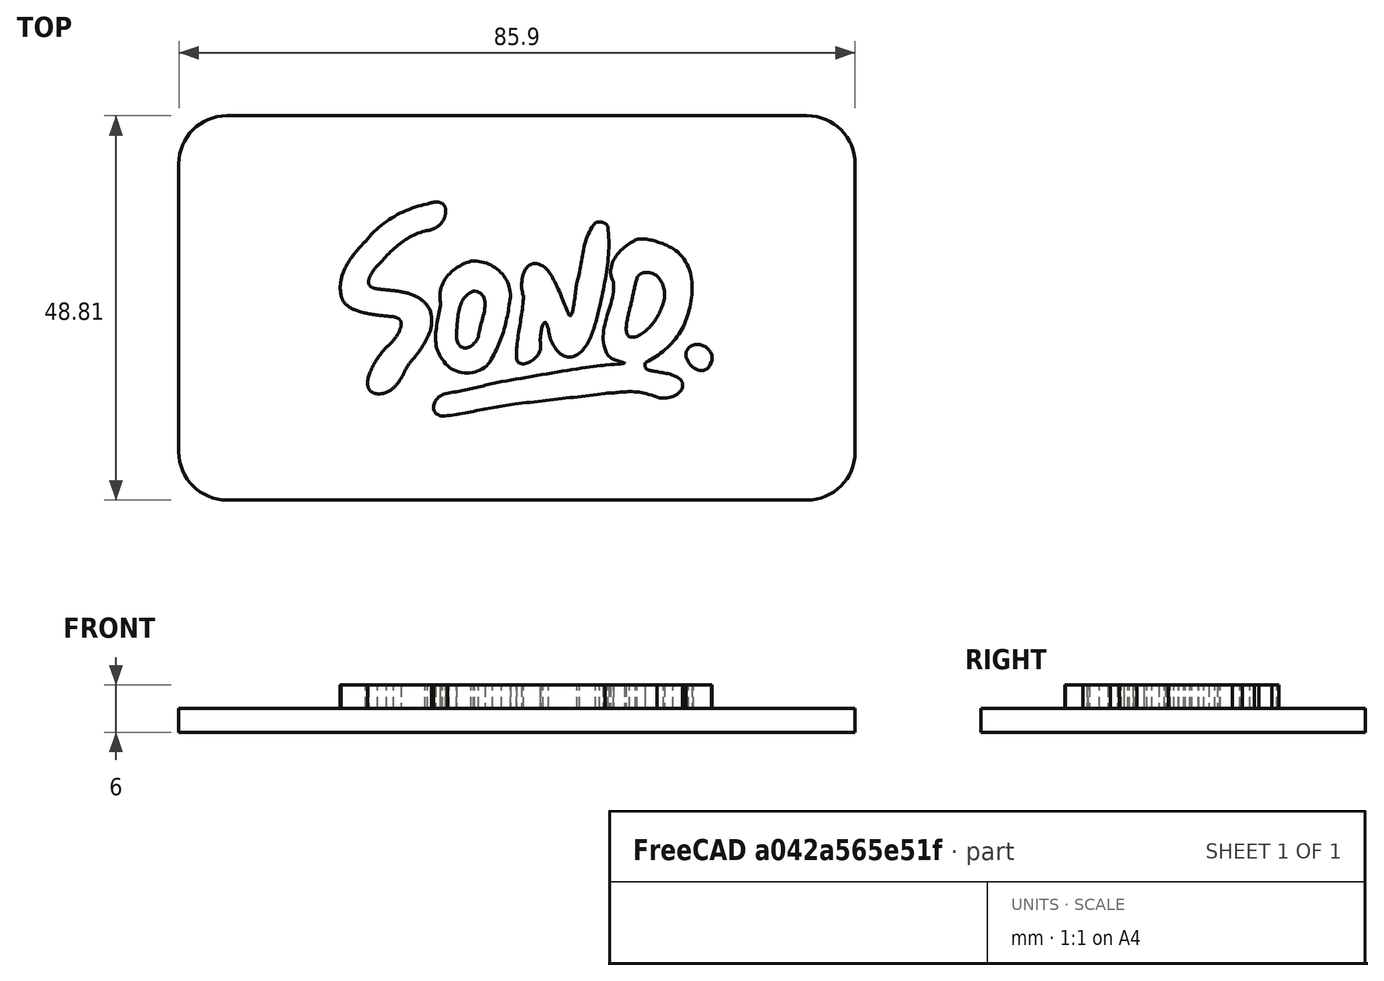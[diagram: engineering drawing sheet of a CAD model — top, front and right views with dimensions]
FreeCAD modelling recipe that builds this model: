
FCSTD DOCUMENT  (FreeCAD 0.22R37841 (Git))
Label: Sono
License: All rights reserved
LicenseURL: http://en.wikipedia.org/wiki/All_rights_reserved
objects: Sketcher::SketchObject×2, PartDesign::Pad×2, PartDesign::Body×1
note: 7 computed .brp shape members not serialized (recipe doc carries the construction recipe); baked Part::Feature solids carry a one-line shape summary decoded from their .brp

FEATURE [Sketcher::SketchObject] Sketch012
  AttachmentSupport = -> [XY_Plane]
  FullyConstrained = false
  MapMode = 5
  sketch-geometry (10):
    g0: LineSegment StartX=2989.09 StartY=-2800.65 StartZ=0 EndX=2989.09 EndY=-2837.26 EndZ=0
    g1: LineSegment StartX=2995.19 StartY=-2843.36 StartZ=0 EndX=3068.89 EndY=-2843.36 EndZ=0
    g2: LineSegment StartX=3074.99 StartY=-2837.26 StartZ=0 EndX=3074.99 EndY=-2800.65 EndZ=0
    g3: LineSegment StartX=3068.89 StartY=-2794.55 StartZ=0 EndX=2995.19 EndY=-2794.55 EndZ=0
    g4: ArcOfCircle CenterX=2995.19 CenterY=-2800.65 CenterZ=0 NormalX=0 NormalY=0 NormalZ=1 AngleXU=0 Radius=6.09984 StartAngle=1.5708 EndAngle=3.14159
    g5: ArcOfCircle CenterX=2995.19 CenterY=-2837.26 CenterZ=0 NormalX=0 NormalY=0 NormalZ=1 AngleXU=0 Radius=6.09984 StartAngle=3.14159 EndAngle=4.71239
    g6: ArcOfCircle CenterX=3068.89 CenterY=-2837.26 CenterZ=0 NormalX=0 NormalY=0 NormalZ=1 AngleXU=0 Radius=6.09984 StartAngle=4.71239 EndAngle=6.28319
    g7: ArcOfCircle CenterX=3068.89 CenterY=-2800.65 CenterZ=0 NormalX=0 NormalY=0 NormalZ=1 AngleXU=0 Radius=6.09984 StartAngle=0 EndAngle=1.5708
    g8: GeomPoint X=2989.09 Y=-2794.55 Z=0
    g9: GeomPoint X=3074.99 Y=-2843.36 Z=0
  constraints (19):
    c: Tangent(g0,g4) = -1.5708
    c: Tangent(g0,g5) = -1.5708
    c: Tangent(g1,g5) = -1.5708
    c: Tangent(g1,g6) = -1.5708
    c: Tangent(g2,g6) = -1.5708
    c: Tangent(g2,g7) = -1.5708
    c: Tangent(g3,g7) = -1.5708
    c: Tangent(g3,g4) = -1.5708
    c: Vertical(g0)
    c: Vertical(g2)
    c: Horizontal(g1)
    c: Horizontal(g3)
    c: Equal(g4,g5)
    c: Equal(g5,g6)
    c: Equal(g6,g7)
    c: PointOnObject(g8,g0)
    c: PointOnObject(g8,g3)
    c: PointOnObject(g9,g1)
    c: PointOnObject(g9,g2)
FEATURE [PartDesign::Pad] Pad
  Direction = (0,0,1)
  Length = 3
  Length2 = 10
  Profile = -> Sketch012
  ReferenceAxis = -> Sketch012 [N_Axis]
  Suppressed = false
  Type = 0
FEATURE [Sketcher::SketchObject] Sketch010
  AttachmentSupport = -> [Pad]
  FullyConstrained = false
  MapMode = 5
  Placement = pos=(0,0,3) rot=(0,0,1;0rad)
  sketch-geometry (73):
    g0: BSplineCurve PolesCount=4 KnotsCount=2 Degree=3 IsPeriodic=0
    g1: BSplineCurve PolesCount=4 KnotsCount=2 Degree=3 IsPeriodic=0
    g2: BSplineCurve PolesCount=4 KnotsCount=2 Degree=3 IsPeriodic=0
    g3: BSplineCurve PolesCount=4 KnotsCount=2 Degree=3 IsPeriodic=0
    g4: BSplineCurve PolesCount=4 KnotsCount=2 Degree=3 IsPeriodic=0
    g5: BSplineCurve PolesCount=4 KnotsCount=2 Degree=3 IsPeriodic=0
    g6: BSplineCurve PolesCount=4 KnotsCount=2 Degree=3 IsPeriodic=0
    g7: BSplineCurve PolesCount=4 KnotsCount=2 Degree=3 IsPeriodic=0
    g8: BSplineCurve PolesCount=4 KnotsCount=2 Degree=3 IsPeriodic=0
    g9: BSplineCurve PolesCount=4 KnotsCount=2 Degree=3 IsPeriodic=0
    g10: BSplineCurve PolesCount=4 KnotsCount=2 Degree=3 IsPeriodic=0
    g11: BSplineCurve PolesCount=4 KnotsCount=2 Degree=3 IsPeriodic=0
    g12: BSplineCurve PolesCount=4 KnotsCount=2 Degree=3 IsPeriodic=0
    g13: BSplineCurve PolesCount=4 KnotsCount=2 Degree=3 IsPeriodic=0
    g14: BSplineCurve PolesCount=4 KnotsCount=2 Degree=3 IsPeriodic=0
    g15: BSplineCurve PolesCount=4 KnotsCount=2 Degree=3 IsPeriodic=0
    g16: BSplineCurve PolesCount=4 KnotsCount=2 Degree=3 IsPeriodic=0
    g17: BSplineCurve PolesCount=4 KnotsCount=2 Degree=3 IsPeriodic=0
    g18: BSplineCurve PolesCount=4 KnotsCount=2 Degree=3 IsPeriodic=0
    g19: BSplineCurve PolesCount=4 KnotsCount=2 Degree=3 IsPeriodic=0
    g20: BSplineCurve PolesCount=4 KnotsCount=2 Degree=3 IsPeriodic=0
    g21: BSplineCurve PolesCount=4 KnotsCount=2 Degree=3 IsPeriodic=0
    g22: BSplineCurve PolesCount=4 KnotsCount=2 Degree=3 IsPeriodic=0
    g23: BSplineCurve PolesCount=4 KnotsCount=2 Degree=3 IsPeriodic=0
    g24: BSplineCurve PolesCount=4 KnotsCount=2 Degree=3 IsPeriodic=0
    g25: BSplineCurve PolesCount=4 KnotsCount=2 Degree=3 IsPeriodic=0
    g26: BSplineCurve PolesCount=4 KnotsCount=2 Degree=3 IsPeriodic=0
    g27: BSplineCurve PolesCount=4 KnotsCount=2 Degree=3 IsPeriodic=0
    g28: BSplineCurve PolesCount=4 KnotsCount=2 Degree=3 IsPeriodic=0
    g29: BSplineCurve PolesCount=4 KnotsCount=2 Degree=3 IsPeriodic=0
    g30: BSplineCurve PolesCount=4 KnotsCount=2 Degree=3 IsPeriodic=0
    g31: BSplineCurve PolesCount=4 KnotsCount=2 Degree=3 IsPeriodic=0
    g32: BSplineCurve PolesCount=4 KnotsCount=2 Degree=3 IsPeriodic=0
    g33: BSplineCurve PolesCount=4 KnotsCount=2 Degree=3 IsPeriodic=0
    g34: BSplineCurve PolesCount=4 KnotsCount=2 Degree=3 IsPeriodic=0
    g35: BSplineCurve PolesCount=4 KnotsCount=2 Degree=3 IsPeriodic=0
    g36: BSplineCurve PolesCount=4 KnotsCount=2 Degree=3 IsPeriodic=0
    g37: BSplineCurve PolesCount=4 KnotsCount=2 Degree=3 IsPeriodic=0
    g38: BSplineCurve PolesCount=4 KnotsCount=2 Degree=3 IsPeriodic=0
    g39: BSplineCurve PolesCount=4 KnotsCount=2 Degree=3 IsPeriodic=0
    g40: BSplineCurve PolesCount=4 KnotsCount=2 Degree=3 IsPeriodic=0
    g41: BSplineCurve PolesCount=4 KnotsCount=2 Degree=3 IsPeriodic=0
    g42: BSplineCurve PolesCount=4 KnotsCount=2 Degree=3 IsPeriodic=0
    g43: BSplineCurve PolesCount=4 KnotsCount=2 Degree=3 IsPeriodic=0
    g44: BSplineCurve PolesCount=4 KnotsCount=2 Degree=3 IsPeriodic=0
    g45: BSplineCurve PolesCount=4 KnotsCount=2 Degree=3 IsPeriodic=0
    g46: BSplineCurve PolesCount=4 KnotsCount=2 Degree=3 IsPeriodic=0
    g47: BSplineCurve PolesCount=4 KnotsCount=2 Degree=3 IsPeriodic=0
    g48: BSplineCurve PolesCount=4 KnotsCount=2 Degree=3 IsPeriodic=0
    g49: BSplineCurve PolesCount=4 KnotsCount=2 Degree=3 IsPeriodic=0
    g50: BSplineCurve PolesCount=4 KnotsCount=2 Degree=3 IsPeriodic=0
    g51: BSplineCurve PolesCount=4 KnotsCount=2 Degree=3 IsPeriodic=0
    g52: BSplineCurve PolesCount=4 KnotsCount=2 Degree=3 IsPeriodic=0
    g53: BSplineCurve PolesCount=4 KnotsCount=2 Degree=3 IsPeriodic=0
    g54: BSplineCurve PolesCount=4 KnotsCount=2 Degree=3 IsPeriodic=0
    g55: BSplineCurve PolesCount=4 KnotsCount=2 Degree=3 IsPeriodic=0
    g56: BSplineCurve PolesCount=4 KnotsCount=2 Degree=3 IsPeriodic=0
    g57: BSplineCurve PolesCount=4 KnotsCount=2 Degree=3 IsPeriodic=0
    g58: BSplineCurve PolesCount=4 KnotsCount=2 Degree=3 IsPeriodic=0
    g59: BSplineCurve PolesCount=4 KnotsCount=2 Degree=3 IsPeriodic=0
    g60: BSplineCurve PolesCount=4 KnotsCount=2 Degree=3 IsPeriodic=0
    g61: BSplineCurve PolesCount=2 KnotsCount=2 Degree=1 IsPeriodic=0
    g62: BSplineCurve PolesCount=4 KnotsCount=2 Degree=3 IsPeriodic=0
    g63: BSplineCurve PolesCount=4 KnotsCount=2 Degree=3 IsPeriodic=0
    g64: BSplineCurve PolesCount=4 KnotsCount=2 Degree=3 IsPeriodic=0
    g65: BSplineCurve PolesCount=4 KnotsCount=2 Degree=3 IsPeriodic=0
    g66: BSplineCurve PolesCount=4 KnotsCount=2 Degree=3 IsPeriodic=0
    g67: BSplineCurve PolesCount=4 KnotsCount=2 Degree=3 IsPeriodic=0
    g68: BSplineCurve PolesCount=4 KnotsCount=2 Degree=3 IsPeriodic=0
    g69: BSplineCurve PolesCount=4 KnotsCount=2 Degree=3 IsPeriodic=0
    g70: BSplineCurve PolesCount=2 KnotsCount=2 Degree=1 IsPeriodic=0
    g71: BSplineCurve PolesCount=4 KnotsCount=2 Degree=3 IsPeriodic=0
    g72: BSplineCurve PolesCount=4 KnotsCount=2 Degree=3 IsPeriodic=0
  constraints (73):
    c: Coincident(g0,g1)
    c: Coincident(g1,g2)
    c: Coincident(g2,g3)
    c: Coincident(g3,g4)
    c: Coincident(g4,g5)
    c: Coincident(g5,g6)
    c: Coincident(g6,g7)
    c: Coincident(g7,g8)
    c: Coincident(g8,g9)
    c: Coincident(g9,g10)
    c: Coincident(g10,g11)
    c: Coincident(g11,g12)
    c: Coincident(g12,g13)
    c: Coincident(g13,g14)
    c: Coincident(g14,g15)
    c: Coincident(g15,g16)
    c: Coincident(g16,g17)
    c: Coincident(g17,g18)
    c: Coincident(g18,g19)
    c: Coincident(g19,g20)
    c: Coincident(g20,g21)
    c: Coincident(g21,g22)
    c: Coincident(g22,g23)
    c: Coincident(g23,g24)
    c: Coincident(g24,g25)
    c: Coincident(g25,g26)
    c: Coincident(g26,g27)
    c: Coincident(g27,g28)
    c: Coincident(g28,g29)
    c: Coincident(g29,g30)
    c: Coincident(g30,g0)
    c: Coincident(g31,g32)
    c: Coincident(g32,g33)
    c: Coincident(g33,g34)
    c: Coincident(g34,g35)
    c: Coincident(g35,g36)
    c: Coincident(g36,g37)
    c: Coincident(g37,g38)
    c: Coincident(g38,g39)
    c: Coincident(g39,g40)
    c: Coincident(g40,g41)
    c: Coincident(g41,g31)
    c: Coincident(g42,g43)
    c: Coincident(g43,g44)
    c: Coincident(g44,g45)
    c: Coincident(g45,g46)
    c: Coincident(g46,g47)
    c: Coincident(g47,g48)
    c: Coincident(g48,g49)
    c: Coincident(g49,g50)
    c: Coincident(g50,g51)
    c: Coincident(g51,g52)
    c: Coincident(g52,g53)
    c: Coincident(g53,g54)
    c: Coincident(g54,g55)
    c: Coincident(g55,g42)
    c: Coincident(g56,g57)
    c: Coincident(g57,g58)
    c: Coincident(g58,g59)
    c: Coincident(g59,g60)
    c: Coincident(g60,g61)
    c: Coincident(g61,g56)
    c: Coincident(g62,g63)
    c: Coincident(g63,g64)
    c: Coincident(g64,g65)
    c: Coincident(g65,g66)
    c: Coincident(g66,g62)
    c: Coincident(g67,g68)
    c: Coincident(g68,g69)
    c: Coincident(g69,g70)
    c: Coincident(g70,g67)
    c: Coincident(g71,g72)
    c: Coincident(g72,g71)
FEATURE [PartDesign::Pad] Pad001
  BaseFeature = -> Pad
  Direction = (0,0,1)
  Length = 3
  Length2 = 10
  Profile = -> Sketch010
  ReferenceAxis = -> Sketch010 [N_Axis]
  Suppressed = false
  Type = 0
FEATURE [PartDesign::Body] Body
  AllowCompound = false
  Group = -> [Sketch010,Sketch012,Pad,Pad001]
  Origin = -> Origin
  Tip = -> Pad001
